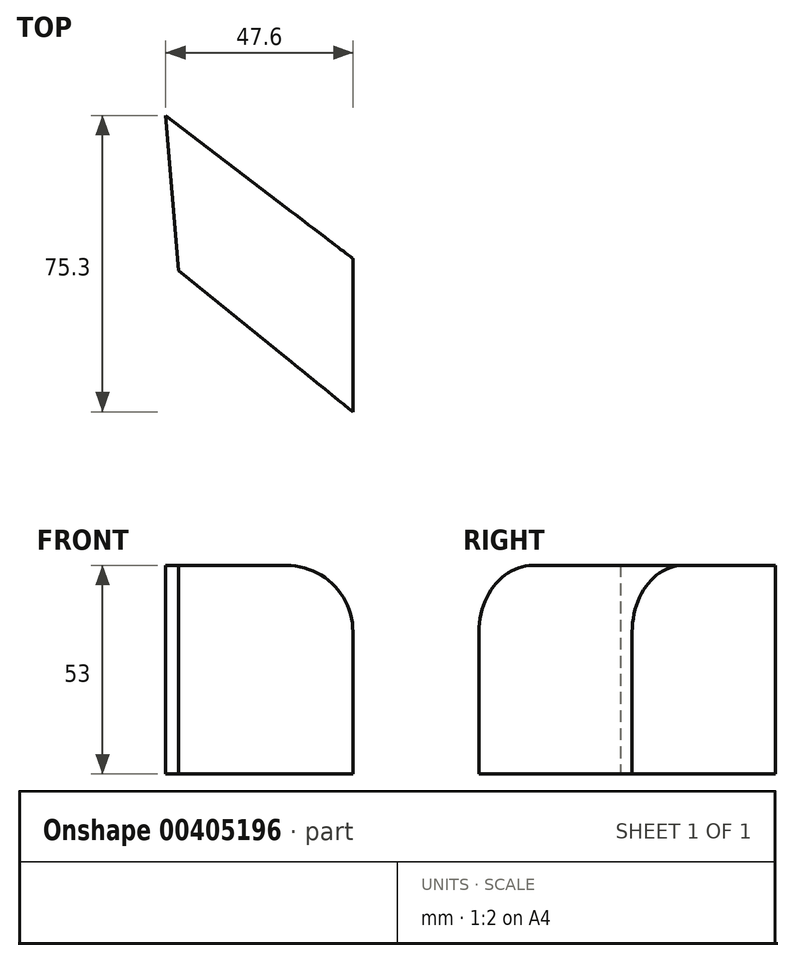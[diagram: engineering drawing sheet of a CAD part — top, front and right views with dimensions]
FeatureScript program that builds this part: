
annotation { "Feature Type Name" : "Feature", "Feature Type Description" : "" }
export const myFeature = defineFeature(function(context is Context, id is Id, definition is map)
    precondition{}
    {
        {
            var Q0;
            Q0=qCreatedBy(makeId("Top.planeOp"),FACE);
            var sketch = newSketch(context, id + "F0", { "sketchPlane" : qUnion([Q0])});
            skLineSegment(sketch, "E0", {"start": v(-93.6, -16.9) * mm, "end": v(-49.23, -52.8) * mm});
            skLineSegment(sketch, "E1", {"start": v(-49.23, -52.8) * mm, "end": v(-49.23, -13.87) * mm});
            skLineSegment(sketch, "E2", {"start": v(-49.23, -13.87) * mm, "end": v(-96.83, 22.5) * mm});
            skLineSegment(sketch, "E3", {"start": v(-96.83, 22.5) * mm, "end": v(-93.6, -16.9) * mm});
            skSolve(sketch);
        }
        {
            var Q0;
            Q0 = qSketchRegion(id + "F0", true);
            extrude(context, id + "F1", {"entities" : qUnion([Q0]), "depth" : 53 * mm});
        }
        {
            var Q0;
            Q0=makeQuery(id+"F1.opExtrude","CAP_EDGE",EDGE,{"disambiguationData":[OSD([sQuery(id+"F0.wireOp",EDGE,"E1")])],"isStart":false});
            fillet(context, id + "F2", {"entities" : qUnion([Q0]), "radius" : 16.9 * mm, "tangentPropagation" : true, "allowEdgeOverflow" : false});
        }
    });
